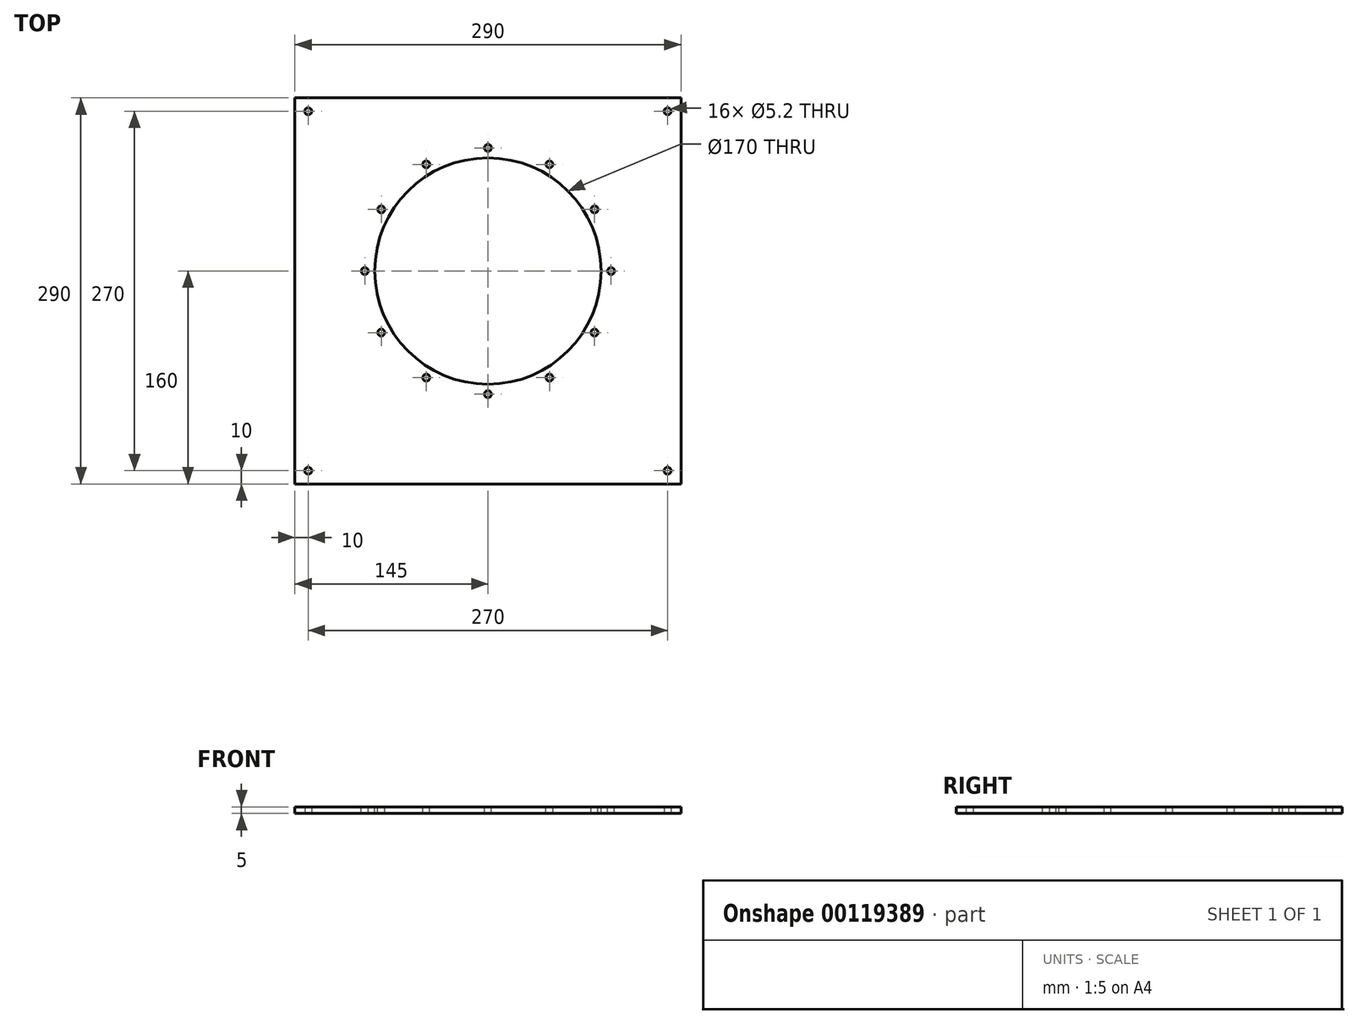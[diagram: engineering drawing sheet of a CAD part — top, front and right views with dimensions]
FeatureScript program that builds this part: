
annotation { "Feature Type Name" : "Feature", "Feature Type Description" : "" }
export const myFeature = defineFeature(function(context is Context, id is Id, definition is map)
    precondition{}
    {
        {
            var Q0;
            Q0=qCreatedBy(makeId("Top.planeOp"),FACE);
            var sketch = newSketch(context, id + "F0", { "sketchPlane" : qUnion([Q0])});
            skLineSegment(sketch, "E0.bottom", {"start": v(145, -145) * mm, "end": v(-145, -145) * mm});
            skLineSegment(sketch, "E0.top", {"start": v(145, 145) * mm, "end": v(-145, 145) * mm});
            skLineSegment(sketch, "E0.left", {"start": v(145, -145) * mm, "end": v(145, 145) * mm});
            skLineSegment(sketch, "E0.right", {"start": v(-145, -145) * mm, "end": v(-145, 145) * mm});
            skPoint(sketch, "E0.middle", {"position": v(0, 0) * mm});
            skCircle(sketch, "E1", {"center": v(-135, 135) * mm, "radius": 2.6 * mm});
            skCircle(sketch, "E2.0.1.0", {"center": v(-135, -135) * mm, "radius": 2.6 * mm});
            skCircle(sketch, "E2.1.0.0", {"center": v(135, 135) * mm, "radius": 2.6 * mm});
            skCircle(sketch, "E2.1.1.0", {"center": v(135, -135) * mm, "radius": 2.6 * mm});
            skLineSegment(sketch, "E2.direction1", {"start": v(-135, 135) * mm, "end": v(135, 135) * mm, "construction": true});
            skLineSegment(sketch, "E2.direction2", {"start": v(-135, 135) * mm, "end": v(-135, -135) * mm, "construction": true});
            skSolve(sketch);
        }
        {
            var Q0;
            Q0=makeQuery(id+"F0.imprint","IMPRINT",FACE,{"disambiguationData":[TD([[makeQuery(id+"F0.imprint","IMPRINT",EDGE,{"derivedFrom":sQuery(id+"F0.wireOp",EDGE,"E0.bottom")}),-1.0]])]});
            extrude(context, id + "F1", {"entities" : qUnion([Q0]), "depth" : 5 * mm});
        }
        {
            var Q0;
            Q0=makeQuery(id+"F1.opExtrude","CAP_FACE",FACE,{"disambiguationData":[OSD([sQuery(id+"F0.wireOp",EDGE,"E0.bottom"),sQuery(id+"F0.wireOp",EDGE,"E0.top"),sQuery(id+"F0.wireOp",EDGE,"E0.left"),sQuery(id+"F0.wireOp",EDGE,"E0.right"),sQuery(id+"F0.wireOp",EDGE,"E1"),sQuery(id+"F0.wireOp",EDGE,"E2.0.1.0"),sQuery(id+"F0.wireOp",EDGE,"E2.1.0.0"),sQuery(id+"F0.wireOp",EDGE,"E2.1.1.0")])],"isStart":false});
            var sketch = newSketch(context, id + "F2", { "sketchPlane" : qUnion([Q0])});
            skPoint(sketch, "E3.middle", {"position": v(0, 0) * mm});
            skPoint(sketch, "E4.visualSharp", {"position": v(-80, 95) * mm});
            skPoint(sketch, "E5.visualSharp", {"position": v(80, 95) * mm});
            skPoint(sketch, "E6.visualSharp", {"position": v(80, -65) * mm});
            skPoint(sketch, "E7.visualSharp", {"position": v(-80, -65) * mm});
            skLineSegment(sketch, "E8", {"start": v(-80, -65) * mm, "end": v(80, 95) * mm, "construction": true});
            skCircle(sketch, "E9", {"center": v(0, 15) * mm, "radius": 85 * mm});
            skSolve(sketch);
        }
        {
            var Q0;
            Q0=makeQuery(id+"F2.imprint","IMPRINT",FACE,{"disambiguationData":[TD([[makeQuery(id+"F2.imprint","IMPRINT",EDGE,{"derivedFrom":sQuery(id+"F2.wireOp",EDGE,"E9")}),1.0]])]});
            extrude(context, id + "F3", {"entities" : qUnion([Q0]), "operationType" : NewBodyOperationType.REMOVE, "endBound" : BoundingType.THROUGH_ALL, "oppositeDirection" : true, "depth" : 25 * mm});
        }
        {
            var Q0;
            Q0=makeQuery(id+"F1.opExtrude","CAP_FACE",FACE,{"disambiguationData":[OSD([sQuery(id+"F0.wireOp",EDGE,"E0.bottom"),sQuery(id+"F0.wireOp",EDGE,"E0.top"),sQuery(id+"F0.wireOp",EDGE,"E0.left"),sQuery(id+"F0.wireOp",EDGE,"E0.right"),sQuery(id+"F0.wireOp",EDGE,"E1"),sQuery(id+"F0.wireOp",EDGE,"E2.0.1.0"),sQuery(id+"F0.wireOp",EDGE,"E2.1.0.0"),sQuery(id+"F0.wireOp",EDGE,"E2.1.1.0")])],"isStart":false});
            var sketch = newSketch(context, id + "F4", { "sketchPlane" : qUnion([Q0])});
            skCircle(sketch, "E10.0", {"center": v(0, 15) * mm, "radius": 85 * mm, "construction": true});
            skCircle(sketch, "E11", {"center": v(0, 15) * mm, "radius": 92.5 * mm, "construction": true});
            skLineSegment(sketch, "E12", {"start": v(0, 15) * mm, "end": v(0, 127.07) * mm, "construction": true});
            skCircle(sketch, "E13", {"center": v(0, 107.5) * mm, "radius": 2.6 * mm});
            skCircle(sketch, "E14.1.0", {"center": v(-46.25, 95.1) * mm, "radius": 2.6 * mm});
            skCircle(sketch, "E14.2.0", {"center": v(-80.1, 61.25) * mm, "radius": 2.6 * mm});
            skCircle(sketch, "E14.3.0", {"center": v(-92.5, 15) * mm, "radius": 2.6 * mm});
            skCircle(sketch, "E14.4.0", {"center": v(-80.1, -31.25) * mm, "radius": 2.6 * mm});
            skCircle(sketch, "E14.5.0", {"center": v(-46.25, -65.1) * mm, "radius": 2.6 * mm});
            skCircle(sketch, "E15.1.6.0", {"center": v(0, -77.5) * mm, "radius": 2.6 * mm});
            skCircle(sketch, "E15.1.7.0", {"center": v(46.25, -65.1) * mm, "radius": 2.6 * mm});
            skCircle(sketch, "E15.1.8.0", {"center": v(80.1, -31.25) * mm, "radius": 2.6 * mm});
            skCircle(sketch, "E15.1.9.0", {"center": v(92.5, 15) * mm, "radius": 2.6 * mm});
            skCircle(sketch, "E15.1.10.0", {"center": v(80.1, 61.25) * mm, "radius": 2.6 * mm});
            skCircle(sketch, "E15.1.11.0", {"center": v(46.25, 95.1) * mm, "radius": 2.6 * mm});
            skSolve(sketch);
        }
        {
            var Q0;
            Q0 = qSketchRegion(id + "F4", true);
            extrude(context, id + "F5", {"entities" : qUnion([Q0]), "operationType" : NewBodyOperationType.REMOVE, "endBound" : BoundingType.THROUGH_ALL, "oppositeDirection" : true, "depth" : 25 * mm});
        }
    });
